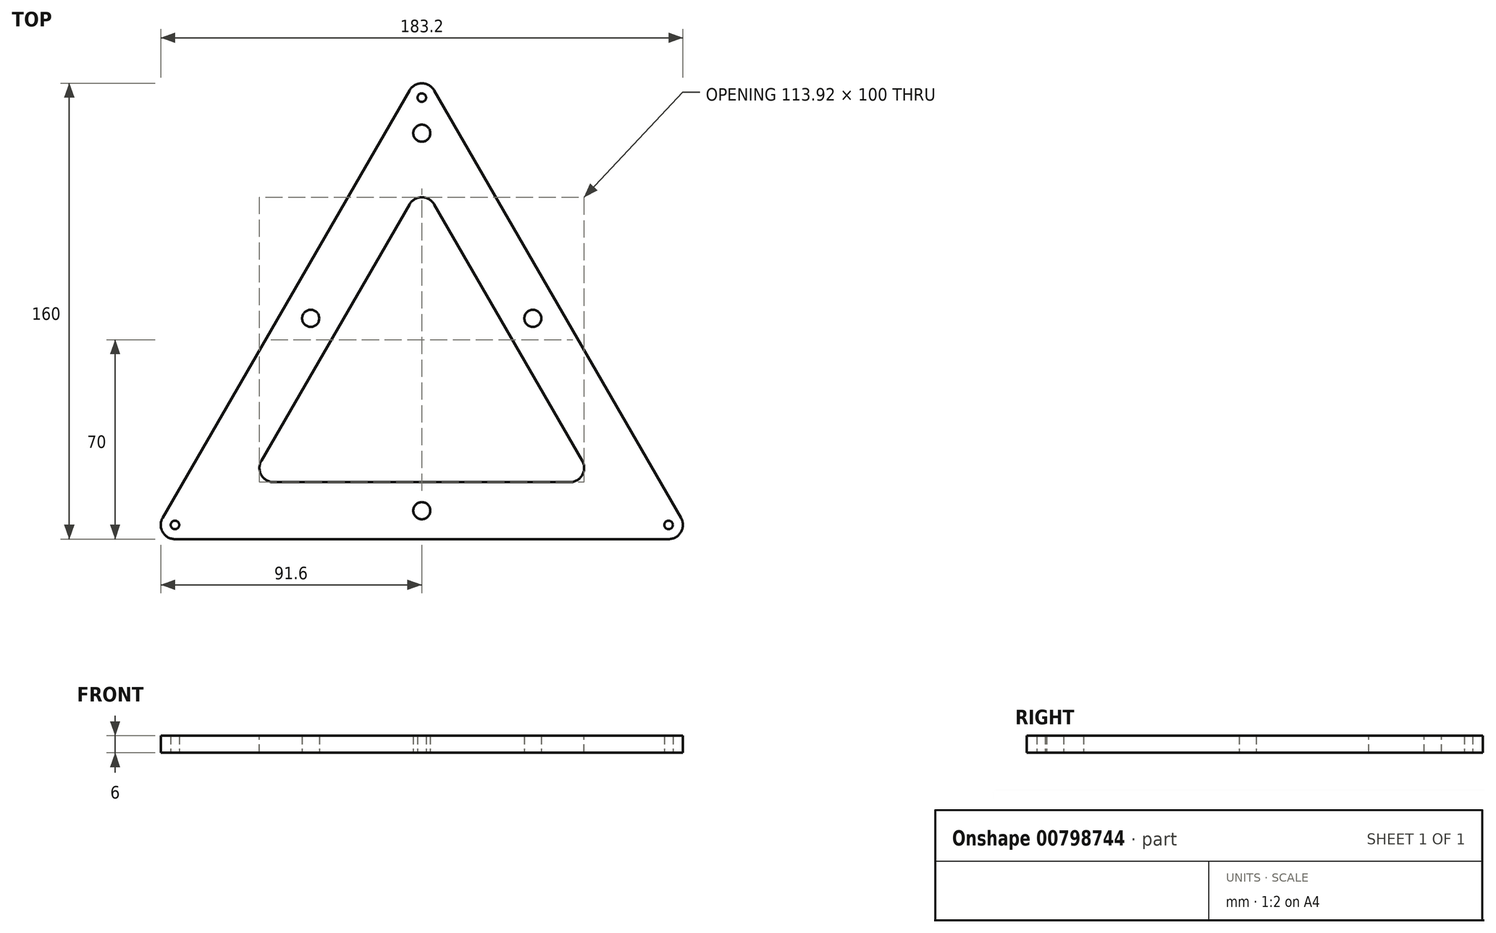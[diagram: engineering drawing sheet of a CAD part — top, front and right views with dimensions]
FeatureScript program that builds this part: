
annotation { "Feature Type Name" : "Feature", "Feature Type Description" : "" }
export const myFeature = defineFeature(function(context is Context, id is Id, definition is map)
    precondition{}
    {
        {
            var Q0;
            Q0=qCreatedBy(makeId("Right.planeOp"),FACE);
            var sketch = newSketch(context, id + "F0", { "sketchPlane" : qUnion([Q0])});
            skLineSegment(sketch, "E0", {"start": v(0, 0) * mm, "end": v(0, 16.51) * mm});
            skSolve(sketch);
        }
        {
            var Q0;
            Q0=qCreatedBy(makeId("Top.planeOp"),FACE);
            var sketch = newSketch(context, id + "F1", { "sketchPlane" : qUnion([Q0])});
            skCircle(sketch, "E1", {"center": v(0, 0) * mm, "radius": 100 * mm, "construction": true});
            skCircle(sketch, "E2", {"center": v(0, 100) * mm, "radius": 5 * mm});
            skCircle(sketch, "E3", {"center": v(-86.6, -50) * mm, "radius": 5 * mm});
            skCircle(sketch, "E4", {"center": v(86.6, -50) * mm, "radius": 5 * mm});
            skLineSegment(sketch, "E5", {"start": v(-86.6, -50) * mm, "end": v(0, 0) * mm, "construction": true});
            skLineSegment(sketch, "E6", {"start": v(86.6, -50) * mm, "end": v(0, 0) * mm, "construction": true});
            skLineSegment(sketch, "E7", {"start": v(-90.93, -47.5) * mm, "end": v(-4.33, 102.5) * mm});
            skLineSegment(sketch, "E8", {"start": v(4.33, 102.5) * mm, "end": v(90.93, -47.5) * mm});
            skLineSegment(sketch, "E9", {"start": v(86.6, -55) * mm, "end": v(-86.6, -55) * mm});
            skLineSegment(sketch, "E10", {"start": v(-60.62, -35) * mm, "end": v(0, 70) * mm});
            skLineSegment(sketch, "E11", {"start": v(0, 70) * mm, "end": v(60.62, -35) * mm});
            skLineSegment(sketch, "E12", {"start": v(60.62, -35) * mm, "end": v(-60.62, -35) * mm});
            skCircle(sketch, "E13", {"center": v(0, 100) * mm, "radius": 1.5 * mm});
            skCircle(sketch, "E14", {"center": v(86.6, -50) * mm, "radius": 1.5 * mm});
            skCircle(sketch, "E15", {"center": v(-86.6, -50) * mm, "radius": 1.5 * mm});
            skCircle(sketch, "E16", {"center": v(0, -45) * mm, "radius": 3 * mm});
            skCircle(sketch, "E17", {"center": v(-38.97, 22.5) * mm, "radius": 3 * mm});
            skCircle(sketch, "E18", {"center": v(38.97, 22.5) * mm, "radius": 3 * mm});
            skSolve(sketch);
        }
        {
            var Q0;
            {var subQ2=sQuery(id+"F1.wireOp",EDGE,"E7");Q0=makeQuery(id+"F1.imprint","IMPRINT",FACE,{"disambiguationData":[TD([[makeQuery(id+"F1.imprint","IMPRINT",EDGE,{"derivedFrom":subQ2}),-1.0]])]});}
            var Q1;
            Q1=makeQuery(id+"F1.imprint","IMPRINT",FACE,{"disambiguationData":[TD([[makeQuery(id+"F1.imprint","IMPRINT",EDGE,{"derivedFrom":sQuery(id+"F1.wireOp",EDGE,"E14")}),-1.0]])]});
            var Q2;
            Q2=makeQuery(id+"F1.imprint","IMPRINT",FACE,{"disambiguationData":[TD([[makeQuery(id+"F1.imprint","IMPRINT",EDGE,{"derivedFrom":sQuery(id+"F1.wireOp",EDGE,"E15")}),-1.0]])]});
            var Q3;
            Q3=makeQuery(id+"F1.imprint","IMPRINT",FACE,{"disambiguationData":[TD([[makeQuery(id+"F1.imprint","IMPRINT",EDGE,{"derivedFrom":sQuery(id+"F1.wireOp",EDGE,"E13")}),-1.0]])]});
            extrude(context, id + "F2", {"entities" : qUnion([Q0, Q1, Q2, Q3]), "depth" : 6 * mm, "offsetDistance" : 25 * mm});
        }
        {
            var Q0;
            Q0=makeQuery(id+"F2.opExtrude","SWEPT_EDGE",EDGE,{"disambiguationData":[OSD([sQuery(id+"F1.wireOp",EDGE,"E10"),sQuery(id+"F1.wireOp",EDGE,"E11")])]});
            var Q1;
            Q1=makeQuery(id+"F2.opExtrude","SWEPT_EDGE",EDGE,{"disambiguationData":[OSD([sQuery(id+"F1.wireOp",EDGE,"E10"),sQuery(id+"F1.wireOp",EDGE,"E12")])]});
            var Q2;
            Q2=makeQuery(id+"F2.opExtrude","SWEPT_EDGE",EDGE,{"disambiguationData":[OSD([sQuery(id+"F1.wireOp",EDGE,"E11"),sQuery(id+"F1.wireOp",EDGE,"E12")])]});
            fillet(context, id + "F3", {"entities" : qUnion([Q0, Q1, Q2]), "radius" : 5 * mm, "tangentPropagation" : true, "allowEdgeOverflow" : false});
        }
        {
            var Q0;
            Q0=qCreatedBy(makeId("Top.planeOp"),FACE);
            var sketch = newSketch(context, id + "F4", { "sketchPlane" : qUnion([Q0])});
            skCircle(sketch, "E19", {"center": v(0, 0) * mm, "radius": 87.5 * mm, "construction": true});
            skCircle(sketch, "E20", {"center": v(0, 87.5) * mm, "radius": 3 * mm});
            skSolve(sketch);
        }
        {
            var Q0;
            Q0=qSketchRegion(id+"F4",true);
            extrude(context, id + "F5", {"entities" : qUnion([Q0]), "operationType" : NewBodyOperationType.REMOVE, "endBound" : BoundingType.SYMMETRIC, "oppositeDirection" : true, "depth" : 25 * mm, "offsetDistance" : 25 * mm});
        }
    });
